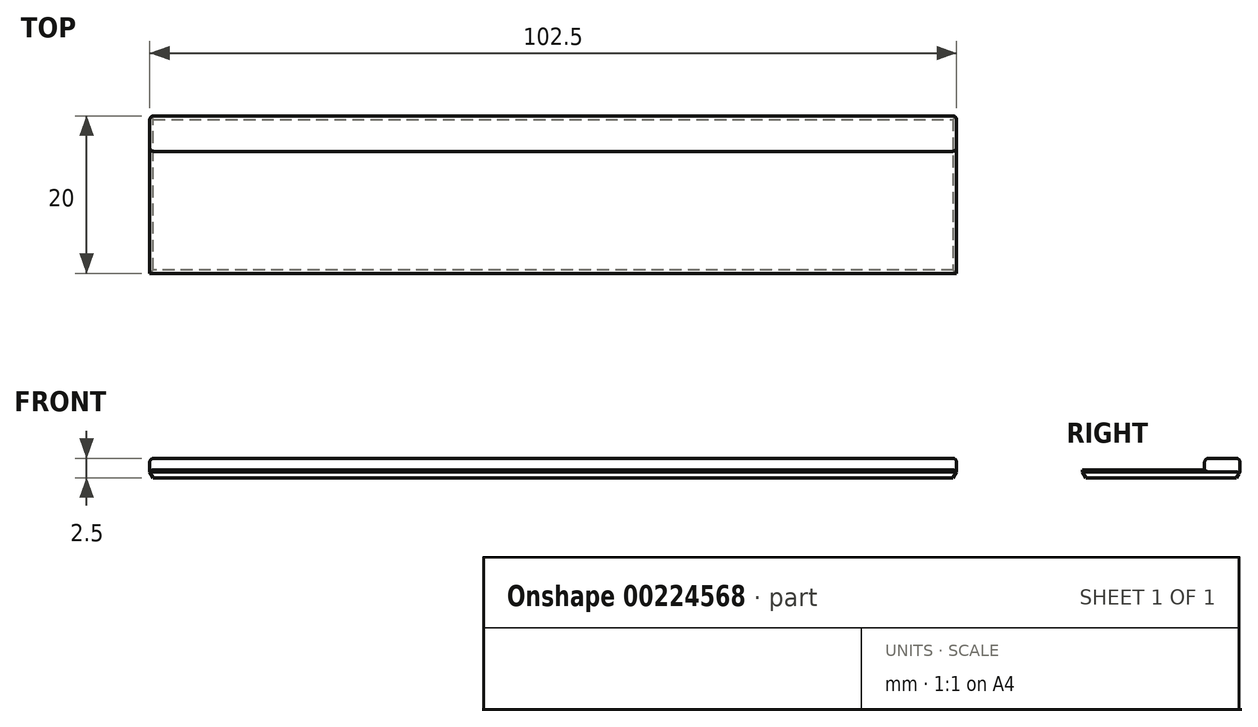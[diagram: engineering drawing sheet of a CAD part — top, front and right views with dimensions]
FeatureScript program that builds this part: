
annotation { "Feature Type Name" : "Feature", "Feature Type Description" : "" }
export const myFeature = defineFeature(function(context is Context, id is Id, definition is map)
    precondition{}
    {
        {
            var Q0;
            Q0=qCreatedBy(makeId("Top.planeOp"),FACE);
            var sketch = newSketch(context, id + "F0", { "sketchPlane" : qUnion([Q0])});
            skLineSegment(sketch, "E0.bottom", {"start": v(0, 0) * mm, "end": v(-102.5, 0) * mm});
            skLineSegment(sketch, "E0.top", {"start": v(0, 20) * mm, "end": v(-102.5, 20) * mm});
            skLineSegment(sketch, "E0.left", {"start": v(0, 0) * mm, "end": v(0, 20) * mm});
            skLineSegment(sketch, "E0.right", {"start": v(-102.5, 0) * mm, "end": v(-102.5, 20) * mm});
            skSolve(sketch);
        }
        {
            var Q0;
            Q0 = qSketchRegion(id + "F0", true);
            extrude(context, id + "F1", {"entities" : qUnion([Q0]), "depth" : 1 * mm});
        }
        {
            var Q0;
            Q0=makeQuery(id+"F1.opExtrude","CAP_FACE",FACE,{"disambiguationData":[OSD([sQuery(id+"F0.wireOp",EDGE,"E0.bottom"),sQuery(id+"F0.wireOp",EDGE,"E0.top"),sQuery(id+"F0.wireOp",EDGE,"E0.left"),sQuery(id+"F0.wireOp",EDGE,"E0.right")])],"isStart":false});
            var sketch = newSketch(context, id + "F2", { "sketchPlane" : qUnion([Q0])});
            skLineSegment(sketch, "E1.bottom", {"start": v(-102.5, 15.5) * mm, "end": v(0, 15.5) * mm});
            skLineSegment(sketch, "E1.top", {"start": v(-102.5, 20) * mm, "end": v(0, 20) * mm});
            skLineSegment(sketch, "E1.left", {"start": v(-102.5, 15.5) * mm, "end": v(-102.5, 20) * mm});
            skLineSegment(sketch, "E1.right", {"start": v(0, 15.5) * mm, "end": v(0, 20) * mm});
            skSolve(sketch);
        }
        {
            var Q0;
            Q0 = qSketchRegion(id + "F2", true);
            extrude(context, id + "F3", {"entities" : qUnion([Q0]), "operationType" : NewBodyOperationType.ADD, "depth" : 1.5 * mm});
        }
        {
            var Q0;
            Q0=makeQuery(id+"F1.opExtrude","CAP_FACE",FACE,{"disambiguationData":[OSD([sQuery(id+"F0.wireOp",EDGE,"E0.bottom"),sQuery(id+"F0.wireOp",EDGE,"E0.top"),sQuery(id+"F0.wireOp",EDGE,"E0.left"),sQuery(id+"F0.wireOp",EDGE,"E0.right")])],"isStart":true});
            chamfer(context, id + "F4", {"entities" : qUnion([Q0]), "chamferType" : ChamferType.OFFSET_ANGLE, "width" : .45 * mm, "oppositeDirection" : false, "angle" : 60 * degree, "tangentPropagation" : true});
        }
        {
            var Q0;
            Q0=makeQuery(id+"F3.boolean.opBoolean","MERGE",EDGE,{"derivedFrom":[makeQuery(id+"F1.opExtrude","SWEPT_EDGE",EDGE,{"disambiguationData":[OSD([sQuery(id+"F0.wireOp",EDGE,"E0.top"),sQuery(id+"F0.wireOp",EDGE,"E0.right")])]}),makeQuery(id+"F3.opExtrude","SWEPT_EDGE",EDGE,{"disambiguationData":[OSD([sQuery(id+"F2.wireOp",EDGE,"E1.top"),sQuery(id+"F2.wireOp",EDGE,"E1.left")])]})]});
            var Q1;
            Q1=makeQuery(id+"F3.opExtrude","SWEPT_EDGE",EDGE,{"disambiguationData":[OSD([sQuery(id+"F0.wireOp",EDGE,"E0.right"),sQuery(id+"F2.wireOp",EDGE,"E1.bottom"),sQuery(id+"F2.wireOp",EDGE,"E1.left")])]});
            var Q2;
            Q2=makeQuery(id+"F3.boolean.opBoolean","MERGE",EDGE,{"derivedFrom":[makeQuery(id+"F1.opExtrude","SWEPT_EDGE",EDGE,{"disambiguationData":[OSD([sQuery(id+"F0.wireOp",EDGE,"E0.top"),sQuery(id+"F0.wireOp",EDGE,"E0.left")])]}),makeQuery(id+"F3.opExtrude","SWEPT_EDGE",EDGE,{"disambiguationData":[OSD([sQuery(id+"F2.wireOp",EDGE,"E1.top"),sQuery(id+"F2.wireOp",EDGE,"E1.right")])]})]});
            var Q3;
            Q3=makeQuery(id+"F3.opExtrude","CAP_EDGE",EDGE,{"disambiguationData":[OSD([sQuery(id+"F2.wireOp",EDGE,"E1.left")])],"isStart":false});
            var Q4;
            Q4=makeQuery(id+"F3.opExtrude","CAP_EDGE",EDGE,{"disambiguationData":[OSD([sQuery(id+"F2.wireOp",EDGE,"E1.top")])],"isStart":false});
            var Q5;
            Q5=makeQuery(id+"F1.opExtrude","CAP_EDGE",EDGE,{"disambiguationData":[OSD([sQuery(id+"F0.wireOp",EDGE,"E0.right")])],"isStart":false});
            var Q6;
            Q6=makeQuery(id+"F3.opExtrude","SWEPT_EDGE",EDGE,{"disambiguationData":[OSD([sQuery(id+"F0.wireOp",EDGE,"E0.left"),sQuery(id+"F2.wireOp",EDGE,"E1.bottom"),sQuery(id+"F2.wireOp",EDGE,"E1.right")])]});
            var Q7;
            Q7=makeQuery(id+"F3.opExtrude","CAP_EDGE",EDGE,{"disambiguationData":[OSD([sQuery(id+"F2.wireOp",EDGE,"E1.right")])],"isStart":false});
            var Q8;
            Q8=makeQuery(id+"F3.opExtrude","CAP_EDGE",EDGE,{"disambiguationData":[OSD([sQuery(id+"F2.wireOp",EDGE,"E1.bottom")])],"isStart":false});
            var Q9;
            Q9=makeQuery(id+"F1.opExtrude","CAP_EDGE",EDGE,{"disambiguationData":[OSD([sQuery(id+"F0.wireOp",EDGE,"E0.left")])],"isStart":false});
            fillet(context, id + "F5", {"entities" : qUnion([Q0, Q1, Q2, Q3, Q4, Q5, Q6, Q7, Q8, Q9]), "radius" : .5 * mm, "tangentPropagation" : true, "allowEdgeOverflow" : false});
        }
    });
